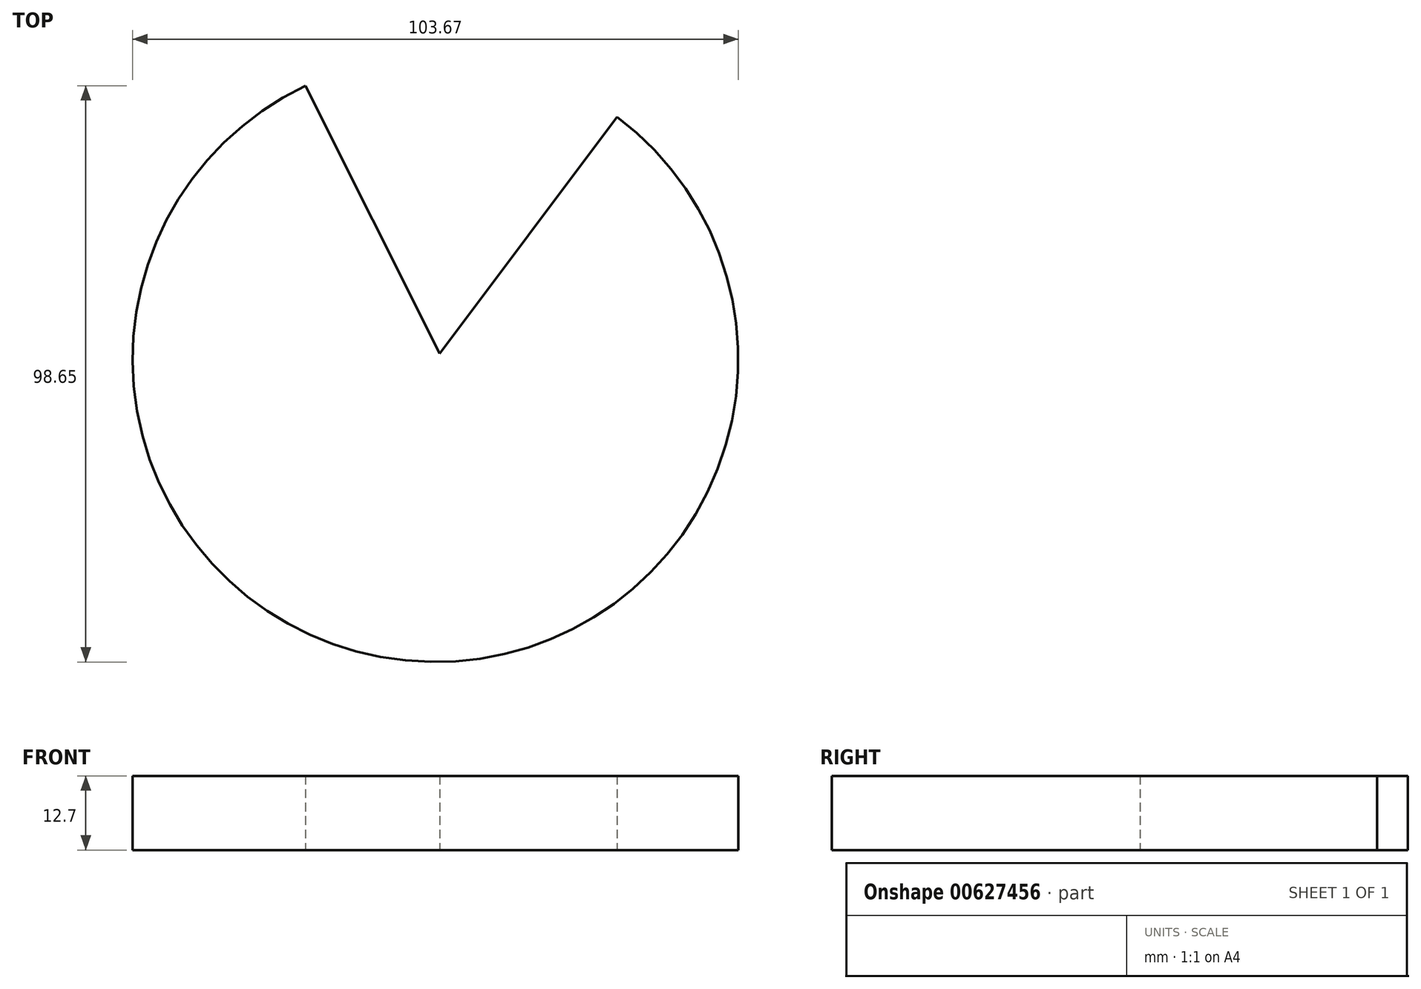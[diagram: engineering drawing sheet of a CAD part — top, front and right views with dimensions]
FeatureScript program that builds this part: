
annotation { "Feature Type Name" : "Feature", "Feature Type Description" : "" }
export const myFeature = defineFeature(function(context is Context, id is Id, definition is map)
    precondition{}
    {
        {
            var Q0;
            Q0=qCreatedBy(makeId("Top.planeOp"),FACE);
            var sketch = newSketch(context, id + "F0", { "sketchPlane" : qUnion([Q0])});
            skArc(sketch, "E0", {"start": v(-23.15, 46.15) * mm, "mid": v(-6, -52.24) * mm, "end": v(30.19, 40.84) * mm});
            skLineSegment(sketch, "E1", {"start": v(0, 0) * mm, "end": v(-23.15, 46.15) * mm});
            skLineSegment(sketch, "E2", {"start": v(-0.88, -0.66) * mm, "end": v(30.19, 40.84) * mm});
            skSolve(sketch);
        }
        {
            var Q0;
            {var subQ0=sQuery(id+"F0.wireOp",EDGE,"E0");Q0=makeQuery(id+"F0.imprint","IMPRINT",FACE,{"disambiguationData":[TD([[makeQuery(id+"F0.imprint","IMPRINT",EDGE,{"derivedFrom":subQ0}),1.0]])]});}
            extrude(context, id + "F1", {"entities" : qUnion([Q0]), "depth" : 12.7 * mm, "offsetDistance" : 25.4 * mm});
        }
    });
